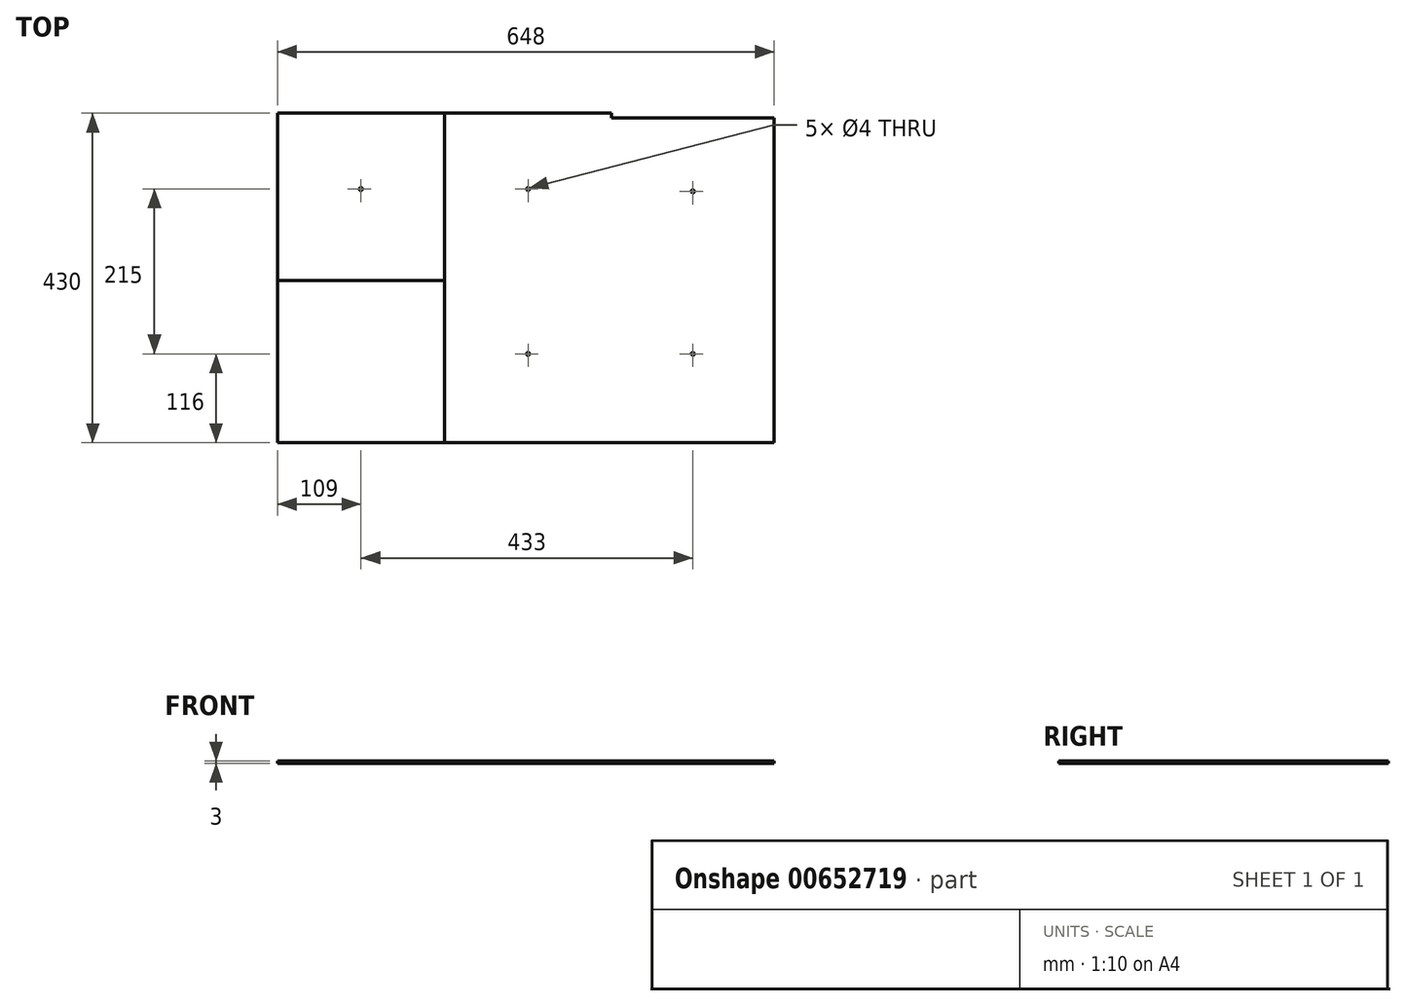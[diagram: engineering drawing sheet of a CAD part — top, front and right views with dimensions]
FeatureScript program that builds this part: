
annotation { "Feature Type Name" : "Feature", "Feature Type Description" : "" }
export const myFeature = defineFeature(function(context is Context, id is Id, definition is map)
    precondition{}
    {
        {
            var Q0;
            Q0=qCreatedBy(makeId("Top.planeOp"),FACE);
            var sketch = newSketch(context, id + "F0", { "sketchPlane" : qUnion([Q0])});
            skLineSegment(sketch, "E0", {"start": v(-324, 215) * mm, "end": v(-324, -3) * mm});
            skLineSegment(sketch, "E1", {"start": v(-324, -3) * mm, "end": v(-106, -3) * mm});
            skLineSegment(sketch, "E2", {"start": v(-106, -3) * mm, "end": v(-106, 215) * mm});
            skLineSegment(sketch, "E3", {"start": v(-106, 215) * mm, "end": v(-324, 215) * mm});
            skLineSegment(sketch, "E4", {"start": v(-106, 215) * mm, "end": v(112, 215) * mm});
            skLineSegment(sketch, "E5", {"start": v(112, 215) * mm, "end": v(112, -3) * mm});
            skLineSegment(sketch, "E6", {"start": v(112, -3) * mm, "end": v(-106, -3) * mm});
            skLineSegment(sketch, "E7", {"start": v(112, 209) * mm, "end": v(324, 209) * mm});
            skLineSegment(sketch, "E8", {"start": v(324, 209) * mm, "end": v(324, -3) * mm});
            skLineSegment(sketch, "E9", {"start": v(324, -3) * mm, "end": v(112, -3) * mm});
            skLineSegment(sketch, "E10", {"start": v(324, -3) * mm, "end": v(324, -215) * mm});
            skLineSegment(sketch, "E11", {"start": v(324, -215) * mm, "end": v(112, -215) * mm});
            skLineSegment(sketch, "E12", {"start": v(-324, -3) * mm, "end": v(-324, -215) * mm});
            skLineSegment(sketch, "E13", {"start": v(-324, -215) * mm, "end": v(-106, -215) * mm});
            skLineSegment(sketch, "E14", {"start": v(-106, -215) * mm, "end": v(-106, -3) * mm});
            skLineSegment(sketch, "E15", {"start": v(-106, -215) * mm, "end": v(112, -215) * mm});
            skLineSegment(sketch, "E16", {"start": v(112, -215) * mm, "end": v(112, -3) * mm});
            skLineSegment(sketch, "E17", {"start": v(-215, 215) * mm, "end": v(-215, -215) * mm, "construction": true});
            skLineSegment(sketch, "E18", {"start": v(-109, -3) * mm, "end": v(-106, 3) * mm, "construction": true});
            skLineSegment(sketch, "E19", {"start": v(-324, -109) * mm, "end": v(-106, -109) * mm, "construction": true});
            skLineSegment(sketch, "E20", {"start": v(112, -109) * mm, "end": v(-106, -109) * mm, "construction": true});
            skLineSegment(sketch, "E21", {"start": v(112, -109) * mm, "end": v(324, -109) * mm, "construction": true});
            skLineSegment(sketch, "E22", {"start": v(218, -215) * mm, "end": v(218, -3) * mm, "construction": true});
            skLineSegment(sketch, "E23", {"start": v(218, -3) * mm, "end": v(218, 209) * mm, "construction": true});
            skLineSegment(sketch, "E24", {"start": v(324, 103) * mm, "end": v(112, 103) * mm, "construction": true});
            skCircle(sketch, "E25", {"center": v(-523.8, 16.07) * mm, "radius": 2 * mm});
            skLineSegment(sketch, "E26", {"start": v(-106, -3) * mm, "end": v(112, -215) * mm, "construction": true});
            skLineSegment(sketch, "E27", {"start": v(-106, -215) * mm, "end": v(112, -3) * mm, "construction": true});
            skLineSegment(sketch, "E28", {"start": v(-106, 215) * mm, "end": v(112, -3) * mm, "construction": true});
            skLineSegment(sketch, "E29", {"start": v(112, 215) * mm, "end": v(-106, -3) * mm, "construction": true});
            skLineSegment(sketch, "E30", {"start": v(3, 215) * mm, "end": v(3, -215) * mm, "construction": true});
            skLineSegment(sketch, "E31", {"start": v(3, 106) * mm, "end": v(112, 106) * mm, "construction": true});
            skLineSegment(sketch, "E32", {"start": v(112, 106) * mm, "end": v(-324, 106) * mm, "construction": true});
            skCircle(sketch, "E33", {"center": v(-215, 116) * mm, "radius": 2 * mm});
            skCircle(sketch, "E34", {"center": v(3, 116) * mm, "radius": 2 * mm});
            skCircle(sketch, "E35", {"center": v(218, 113) * mm, "radius": 2 * mm});
            skCircle(sketch, "E36", {"center": v(218, -99) * mm, "radius": 2 * mm});
            skCircle(sketch, "E37", {"center": v(3, -99) * mm, "radius": 2 * mm});
            skSolve(sketch);
        }
        {
            var Q0;
            Q0=makeQuery(id+"F0.imprint","IMPRINT",FACE,{"disambiguationData":[TD([[makeQuery(id+"F0.imprint","IMPRINT",EDGE,{"derivedFrom":sQuery(id+"F0.wireOp",EDGE,"E0")}),1.0]])]});
            extrude(context, id + "F1", {"entities" : qUnion([Q0]), "depth" : 3 * mm, "offsetDistance" : 25 * mm});
        }
        {
            var Q0;
            Q0=makeQuery(id+"F0.imprint","IMPRINT",FACE,{"disambiguationData":[TD([[makeQuery(id+"F0.imprint","IMPRINT",EDGE,{"derivedFrom":sQuery(id+"F0.wireOp",EDGE,"E2")}),-1.0]])]});
            extrude(context, id + "F2", {"entities" : qUnion([Q0]), "depth" : 3 * mm, "offsetDistance" : 25 * mm});
        }
        {
            var Q0;
            {var subQ1=sQuery(id+"F0.wireOp",EDGE,"E7");Q0=makeQuery(id+"F0.imprint","IMPRINT",FACE,{"disambiguationData":[TD([[makeQuery(id+"F0.imprint","IMPRINT",EDGE,{"derivedFrom":subQ1}),-1.0]])]});}
            extrude(context, id + "F3", {"entities" : qUnion([Q0]), "depth" : 3 * mm, "offsetDistance" : 25 * mm});
        }
        {
            var Q0;
            Q0=makeQuery(id+"F0.imprint","IMPRINT",FACE,{"disambiguationData":[TD([[makeQuery(id+"F0.imprint","IMPRINT",EDGE,{"derivedFrom":sQuery(id+"F0.wireOp",EDGE,"E1")}),-1.0]])]});
            extrude(context, id + "F4", {"entities" : qUnion([Q0]), "depth" : 3 * mm, "offsetDistance" : 25 * mm});
        }
        {
            var Q0;
            Q0=makeQuery(id+"F0.imprint","IMPRINT",FACE,{"disambiguationData":[TD([[makeQuery(id+"F0.imprint","IMPRINT",EDGE,{"derivedFrom":sQuery(id+"F0.wireOp",EDGE,"E6")}),1.0]])]});
            extrude(context, id + "F5", {"entities" : qUnion([Q0]), "depth" : 3 * mm, "offsetDistance" : 25 * mm});
        }
        {
            var Q0;
            Q0=makeQuery(id+"F0.imprint","IMPRINT",FACE,{"disambiguationData":[TD([[makeQuery(id+"F0.imprint","IMPRINT",EDGE,{"derivedFrom":sQuery(id+"F0.wireOp",EDGE,"E9")}),1.0]])]});
            extrude(context, id + "F6", {"entities" : qUnion([Q0]), "operationType" : NewBodyOperationType.ADD, "depth" : 3 * mm, "offsetDistance" : 25 * mm});
        }
    });
